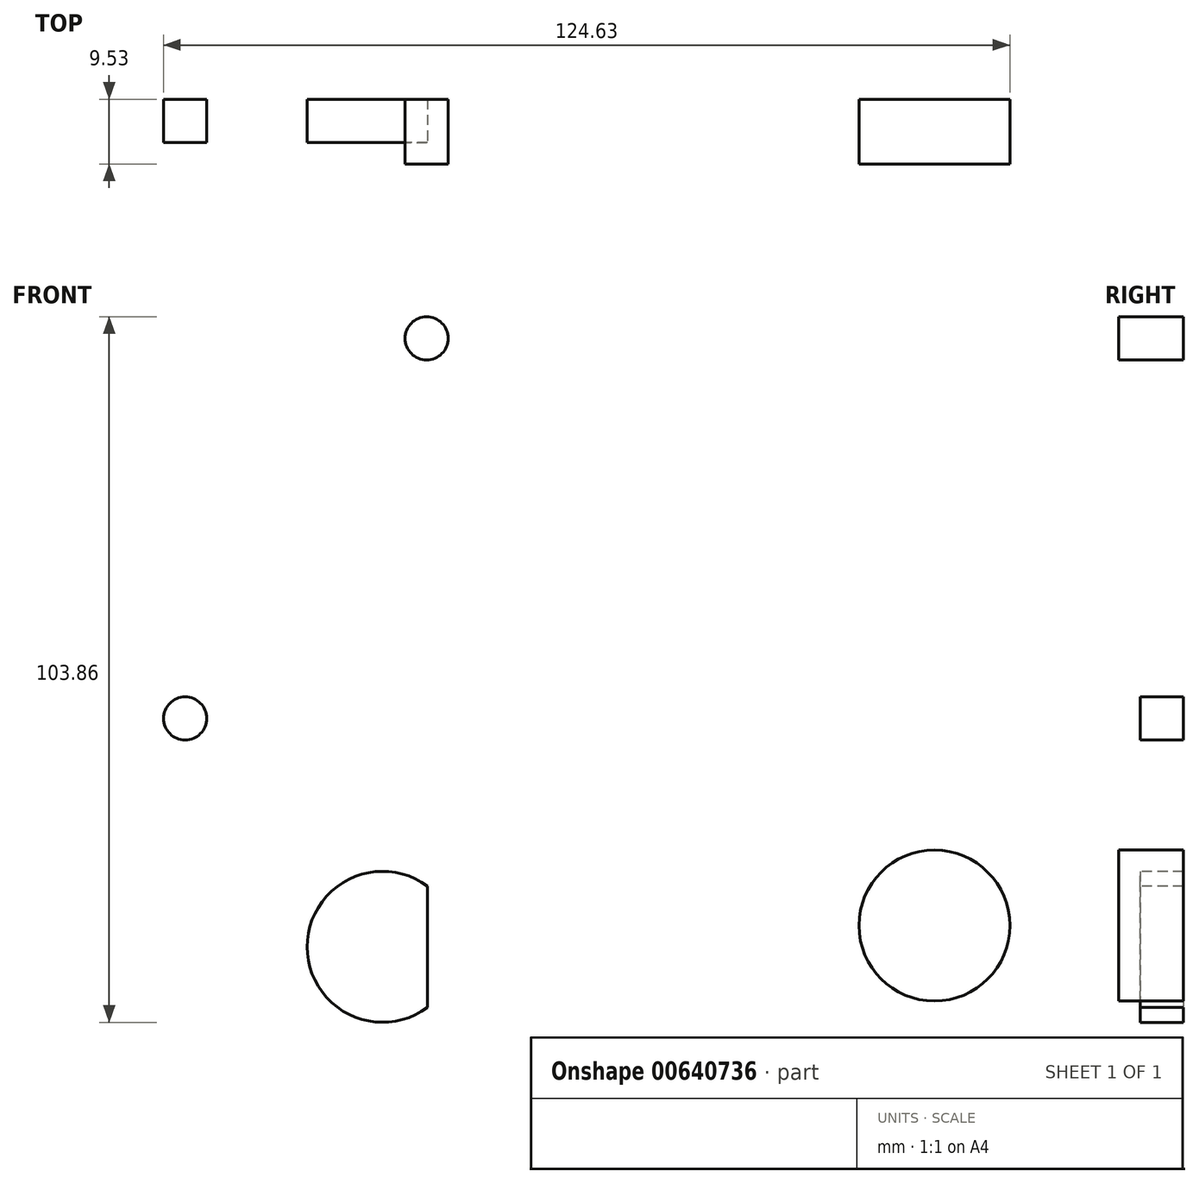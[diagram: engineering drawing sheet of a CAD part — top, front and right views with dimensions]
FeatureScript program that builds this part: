
annotation { "Feature Type Name" : "Feature", "Feature Type Description" : "" }
export const myFeature = defineFeature(function(context is Context, id is Id, definition is map)
    precondition{}
    {
        {
            var Q0;
            Q0=qCreatedBy(makeId("Front.planeOp"),FACE);
            var sketch = newSketch(context, id + "F0", { "sketchPlane" : qUnion([Q0])});
            skCircle(sketch, "E0", {"center": v(0, 0) * mm, "radius": 3.98 * mm});
            skCircle(sketch, "E1", {"center": v(0, 0) * mm, "radius": 15.88 * mm});
            skLineSegment(sketch, "E2", {"start": v(0, 0) * mm, "end": v(57.24, -66.17) * mm, "construction": true});
            skLineSegment(sketch, "E3", {"start": v(57.24, -66.17) * mm, "end": v(-41.54, 48.03) * mm, "construction": true});
            skCircle(sketch, "E4", {"center": v(-41.54, 48.03) * mm, "radius": 11.11 * mm});
            skCircle(sketch, "E5", {"center": v(-41.54, 48.03) * mm, "radius": 3.18 * mm});
            skCircle(sketch, "E6", {"center": v(33.23, -38.42) * mm, "radius": 11.11 * mm});
            skCircle(sketch, "E7", {"center": v(33.23, -38.42) * mm, "radius": 3.18 * mm});
            skCircle(sketch, "E8", {"center": v(26.2, -25.44) * mm, "radius": 3.18 * mm});
            skLineSegment(sketch, "E9", {"start": v(-41.54, 48.03) * mm, "end": v(-75.16, 18.95) * mm, "construction": true});
            skCircle(sketch, "E10", {"center": v(-75.16, 18.95) * mm, "radius": 7.94 * mm});
            skCircle(sketch, "E11", {"center": v(-75.16, 18.95) * mm, "radius": 3.18 * mm});
            skLineSegment(sketch, "E12", {"start": v(0, 0) * mm, "end": v(-79.13, -68.45) * mm, "construction": true});
            skCircle(sketch, "E13", {"center": v(-48.03, -41.54) * mm, "radius": 11.11 * mm});
            skCircle(sketch, "E14", {"center": v(-48.03, -41.54) * mm, "radius": 3.18 * mm});
            skCircle(sketch, "E15", {"center": v(-32.4, -28.03) * mm, "radius": 3.17 * mm});
            skLineSegment(sketch, "E16", {"start": v(-48.03, -41.54) * mm, "end": v(-94.65, 12.36) * mm, "construction": true});
            skCircle(sketch, "E17", {"center": v(-77.1, -7.93) * mm, "radius": 7.94 * mm});
            skCircle(sketch, "E18", {"center": v(-77.1, -7.93) * mm, "radius": 3.18 * mm});
            skLineSegment(sketch, "E19", {"start": v(-80.77, 24.56) * mm, "end": v(-49.4, 55.89) * mm});
            skLineSegment(sketch, "E20", {"start": v(-33.7, 55.9) * mm, "end": v(11.2, 11.26) * mm});
            skLineSegment(sketch, "E21", {"start": v(12.93, 9.21) * mm, "end": v(42.28, -31.97) * mm});
            skLineSegment(sketch, "E22", {"start": v(25.55, -46.45) * mm, "end": v(-10.98, -11.47) * mm});
            skPoint(sketch, "E23.endSnap0", {"position": v(-39.57, -34.23) * mm});
            skLineSegment(sketch, "E24", {"start": v(9.46, -12.75) * mm, "end": v(-41.4, -50.47) * mm});
            skLineSegment(sketch, "E25", {"start": v(-56.93, -48.2) * mm, "end": v(-83.46, -12.68) * mm});
            skLineSegment(sketch, "E26", {"start": v(-11.26, 11.2) * mm, "end": v(-42.42, -20.14) * mm});
            skPoint(sketch, "E26.startSnap0", {"position": v(-11.26, 33.58) * mm});
            skLineSegment(sketch, "E27", {"start": v(-71.49, -2.32) * mm, "end": v(-53.68, -20.15) * mm});
            skArc(sketch, "E28", {"start": v(-53.68, -20.15) * mm, "mid": v(-48.04, -22.49) * mm, "end": v(-42.42, -20.14) * mm});
            skLineSegment(sketch, "E29.trimOffspring", {"start": v(-55.32, -33.11) * mm, "end": v(-55.9, -33.7) * mm});
            skLineSegment(sketch, "E30", {"start": v(-69.36, 13.52) * mm, "end": v(-50.22, 27.74) * mm});
            skLineSegment(sketch, "E31", {"start": v(-12, -10.39) * mm, "end": v(-39.1, 26.1) * mm});
            skArc(sketch, "E32", {"start": v(-39.1, 26.1) * mm, "mid": v(-44.32, 29.22) * mm, "end": v(-50.22, 27.74) * mm});
            skLineSegment(sketch, "E33.trimOffspring", {"start": v(-49.97, 40.74) * mm, "end": v(-50.46, 41.4) * mm});
            skSolve(sketch);
        }
        {
            var Q0;
            {var subQ4=sQuery(id+"F0.wireOp",EDGE,"E19");Q0=makeQuery(id+"F0.imprint","IMPRINT",FACE,{"disambiguationData":[TD([[makeQuery(id+"F0.imprint","IMPRINT",EDGE,{"derivedFrom":subQ4}),-1.0]])]});}
            var Q1;
            Q1=makeQuery(id+"F0.imprint","IMPRINT",FACE,{"disambiguationData":[TD([[makeQuery(id+"F0.imprint","IMPRINT",EDGE,{"derivedFrom":sQuery(id+"F0.wireOp",EDGE,"E5")}),-1.0]])]});
            var Q2;
            Q2=makeQuery(id+"F0.imprint","IMPRINT",FACE,{"disambiguationData":[TD([[makeQuery(id+"F0.imprint","IMPRINT",EDGE,{"derivedFrom":sQuery(id+"F0.wireOp",EDGE,"E11")}),-1.0]])]});
            var Q3;
            Q3=makeQuery(id+"F0.imprint","IMPRINT",FACE,{"disambiguationData":[TD([[makeQuery(id+"F0.imprint","IMPRINT",EDGE,{"derivedFrom":sQuery(id+"F0.wireOp",EDGE,"E0")}),-1.0]])]});
            var Q4;
            {var subQ0=sQuery(id+"F0.wireOp",EDGE,"E26");var subQ1=sQuery(id+"F0.wireOp",EDGE,"E1");var subQ2=makeQuery(id+"F0.imprint","INTERSECT",VERTEX,{"derivedFrom":[subQ1,subQ0]});Q4=makeQuery(id+"F0.imprint","IMPRINT",FACE,{"disambiguationData":[TD([[makeQuery(id+"F0.imprint","IMPRINT",EDGE,{"disambiguationData":[TD([[subQ2,-1.0]])],"derivedFrom":subQ1}),-1.0]])]});}
            var Q5;
            {var subQ0=sQuery(id+"F0.wireOp",EDGE,"E22");var subQ1=sQuery(id+"F0.wireOp",EDGE,"E1");var subQ2=makeQuery(id+"F0.imprint","INTERSECT",VERTEX,{"derivedFrom":[subQ1,subQ0]});Q5=makeQuery(id+"F0.imprint","IMPRINT",FACE,{"disambiguationData":[TD([[makeQuery(id+"F0.imprint","IMPRINT",EDGE,{"disambiguationData":[TD([[subQ2,-1.0]])],"derivedFrom":subQ1}),-1.0]])]});}
            var Q6;
            Q6=makeQuery(id+"F0.imprint","IMPRINT",FACE,{"disambiguationData":[TD([[makeQuery(id+"F0.imprint","IMPRINT",EDGE,{"derivedFrom":sQuery(id+"F0.wireOp",EDGE,"E8")}),-1.0]])]});
            var Q7;
            Q7=makeQuery(id+"F0.imprint","IMPRINT",FACE,{"disambiguationData":[TD([[makeQuery(id+"F0.imprint","IMPRINT",EDGE,{"derivedFrom":sQuery(id+"F0.wireOp",EDGE,"E7")}),-1.0]])]});
            extrude(context, id + "F1", {"entities" : qUnion([Q0, Q1, Q2, Q3, Q4, Q5, Q6, Q7]), "depth" : 3.17 * mm, "offsetDistance" : 25.4 * mm});
        }
        {
            var Q0;
            Q0=makeQuery(id+"F0.imprint","IMPRINT",FACE,{"disambiguationData":[TD([[makeQuery(id+"F0.imprint","IMPRINT",EDGE,{"derivedFrom":sQuery(id+"F0.wireOp",EDGE,"E15")}),-1.0]])]});
            var Q1;
            Q1=makeQuery(id+"F0.imprint","IMPRINT",FACE,{"disambiguationData":[TD([[makeQuery(id+"F0.imprint","IMPRINT",EDGE,{"derivedFrom":sQuery(id+"F0.wireOp",EDGE,"E14")}),-1.0]])]});
            var Q2;
            Q2=makeQuery(id+"F0.imprint","IMPRINT",FACE,{"disambiguationData":[TD([[makeQuery(id+"F0.imprint","IMPRINT",EDGE,{"derivedFrom":sQuery(id+"F0.wireOp",EDGE,"E18")}),-1.0]])]});
            var Q3;
            {var subQ0=sQuery(id+"F0.wireOp",EDGE,"E22");var subQ1=sQuery(id+"F0.wireOp",EDGE,"E1");var subQ2=makeQuery(id+"F0.imprint","INTERSECT",VERTEX,{"derivedFrom":[subQ1,subQ0]});Q3=makeQuery(id+"F0.imprint","IMPRINT",FACE,{"disambiguationData":[TD([[makeQuery(id+"F0.imprint","IMPRINT",EDGE,{"disambiguationData":[TD([[subQ2,-1.0]])],"derivedFrom":subQ1}),-1.0]])]});}
            var Q4;
            Q4=makeQuery(id+"F0.imprint","IMPRINT",FACE,{"disambiguationData":[TD([[makeQuery(id+"F0.imprint","IMPRINT",EDGE,{"derivedFrom":sQuery(id+"F0.wireOp",EDGE,"E0")}),-1.0]])]});
            var Q5;
            {var subQ0=sQuery(id+"F0.wireOp",EDGE,"E26");var subQ1=sQuery(id+"F0.wireOp",EDGE,"E1");var subQ2=makeQuery(id+"F0.imprint","INTERSECT",VERTEX,{"derivedFrom":[subQ1,subQ0]});Q5=makeQuery(id+"F0.imprint","IMPRINT",FACE,{"disambiguationData":[TD([[makeQuery(id+"F0.imprint","IMPRINT",EDGE,{"disambiguationData":[TD([[subQ2,-1.0]])],"derivedFrom":subQ1}),-1.0]])]});}
            extrude(context, id + "F2", {"entities" : qUnion([Q0, Q1, Q2, Q3, Q4, Q5]), "oppositeDirection" : true, "depth" : 3.17 * mm, "offsetDistance" : 25.4 * mm});
        }
        {
            var Q0;
            Q0=qCreatedBy(makeId("Front.planeOp"),FACE);
            cPlane(context, id + "F3", {"entities" : qUnion([Q0]), "cplaneType" : CPlaneType.OFFSET, "offset" : 9.52 * mm, "oppositeDirection" : true, "width" : 152.4 * mm, "height" : 152.4 * mm});
        }
        {
            var Q0;
            Q0=makeQuery(id+"F2.opExtrude","CAP_FACE",FACE,{"disambiguationData":[OSD([sQuery(id+"F0.wireOp",EDGE,"E0"),sQuery(id+"F0.wireOp",EDGE,"E1"),sQuery(id+"F0.wireOp",EDGE,"E13"),sQuery(id+"F0.wireOp",EDGE,"E14"),sQuery(id+"F0.wireOp",EDGE,"E15"),sQuery(id+"F0.wireOp",EDGE,"E17"),sQuery(id+"F0.wireOp",EDGE,"E18"),sQuery(id+"F0.wireOp",EDGE,"E24"),sQuery(id+"F0.wireOp",EDGE,"E25"),sQuery(id+"F0.wireOp",EDGE,"E26"),sQuery(id+"F0.wireOp",EDGE,"E27"),sQuery(id+"F0.wireOp",EDGE,"E28"),sQuery(id+"F0.wireOp",EDGE,"E31")])],"isStart":false});
            var sketch = newSketch(context, id + "F4", { "sketchPlane" : qUnion([Q0])});
            skCircle(sketch, "E34", {"center": v(48.03, -41.54) * mm, "radius": 11.11 * mm});
            skLineSegment(sketch, "E35", {"start": v(41.4, -50.47) * mm, "end": v(41.4, -32.62) * mm});
            skSolve(sketch);
        }
        {
            var Q0;
            {var subQ0=sQuery(id+"F4.wireOp",EDGE,"E35");Q0=makeQuery(id+"F4.imprint","IMPRINT",FACE,{"disambiguationData":[TD([[makeQuery(id+"F4.imprint","IMPRINT",EDGE,{"derivedFrom":subQ0}),-1.0]])]});}
            var Q1;
            Q1=makeQuery(id+"F4.imprint","IMPRINT",FACE,{"disambiguationData":[TD([[makeQuery(id+"F4.imprint","IMPRINT",EDGE,{"derivedFrom":makeQuery(id+"F2.opExtrude","CAP_EDGE",EDGE,{"disambiguationData":[OSD([sQuery(id+"F0.wireOp",EDGE,"E14")])],"isStart":false})}),-1.0]])]});
            var Q2;
            Q2=makeQuery(id+"F0.imprint","IMPRINT",FACE,{"disambiguationData":[TD([[makeQuery(id+"F0.imprint","IMPRINT",EDGE,{"derivedFrom":sQuery(id+"F0.wireOp",EDGE,"E7")}),-1.0]])]});
            var Q3;
            Q3=makeQuery(id+"F0.imprint","IMPRINT",FACE,{"disambiguationData":[TD([[makeQuery(id+"F0.imprint","IMPRINT",EDGE,{"derivedFrom":sQuery(id+"F0.wireOp",EDGE,"E7")}),1.0]])]});
            var Q4;
            Q4=makeQuery(id+"F0.imprint","IMPRINT",FACE,{"disambiguationData":[TD([[makeQuery(id+"F0.imprint","IMPRINT",EDGE,{"derivedFrom":sQuery(id+"F0.wireOp",EDGE,"E5")}),1.0]])]});
            var Q5;
            Q5=makeQuery(id+"F4.imprint","IMPRINT",FACE,{"disambiguationData":[TD([[makeQuery(id+"F4.imprint","IMPRINT",EDGE,{"derivedFrom":makeQuery(id+"F2.opExtrude","CAP_EDGE",EDGE,{"disambiguationData":[OSD([sQuery(id+"F0.wireOp",EDGE,"E18")])],"isStart":false})}),-1.0]])]});
            var Q6;
            Q6=qCreatedBy(id+"F3.planeOp",FACE);
            extrude(context, id + "F5", {"entities" : qUnion([Q0, Q1, Q2, Q3, Q4, Q5]), "endBound" : BoundingType.UP_TO_SURFACE, "depth" : 25.4 * mm, "endBoundEntityFace" : qUnion([Q6]), "offsetDistance" : 25.4 * mm});
        }
        {
            var Q0;
            Q0=makeQuery(id+"F1.opExtrude","SWEPT_BODY",BODY,{"disambiguationData":[OSD([sQuery(id+"F0.wireOp",EDGE,"E0"),sQuery(id+"F0.wireOp",EDGE,"E1"),sQuery(id+"F0.wireOp",EDGE,"E4"),sQuery(id+"F0.wireOp",EDGE,"E5"),sQuery(id+"F0.wireOp",EDGE,"E6"),sQuery(id+"F0.wireOp",EDGE,"E7"),sQuery(id+"F0.wireOp",EDGE,"E8"),sQuery(id+"F0.wireOp",EDGE,"E10"),sQuery(id+"F0.wireOp",EDGE,"E11"),sQuery(id+"F0.wireOp",EDGE,"E19"),sQuery(id+"F0.wireOp",EDGE,"E20"),sQuery(id+"F0.wireOp",EDGE,"E21"),sQuery(id+"F0.wireOp",EDGE,"E22"),sQuery(id+"F0.wireOp",EDGE,"E30"),sQuery(id+"F0.wireOp",EDGE,"E31"),sQuery(id+"F0.wireOp",EDGE,"E32")])]});
            var Q1;
            Q1=makeQuery(id+"F2.opExtrude","SWEPT_BODY",BODY,{"disambiguationData":[OSD([sQuery(id+"F0.wireOp",EDGE,"E0"),sQuery(id+"F0.wireOp",EDGE,"E1"),sQuery(id+"F0.wireOp",EDGE,"E13"),sQuery(id+"F0.wireOp",EDGE,"E14"),sQuery(id+"F0.wireOp",EDGE,"E15"),sQuery(id+"F0.wireOp",EDGE,"E17"),sQuery(id+"F0.wireOp",EDGE,"E18"),sQuery(id+"F0.wireOp",EDGE,"E24"),sQuery(id+"F0.wireOp",EDGE,"E25"),sQuery(id+"F0.wireOp",EDGE,"E26"),sQuery(id+"F0.wireOp",EDGE,"E27"),sQuery(id+"F0.wireOp",EDGE,"E28"),sQuery(id+"F0.wireOp",EDGE,"E31")])]});
            var Q2;
            Q2=makeQuery(id+"F5.opExtrude","SWEPT_BODY",BODY,{"disambiguationData":[OSD([sQuery(id+"F0.wireOp",EDGE,"E5")])]});
            var Q3;
            Q3=makeQuery(id+"F5.opExtrude","SWEPT_BODY",BODY,{"disambiguationData":[OSD([sQuery(id+"F0.wireOp",EDGE,"E18")])]});
            var Q4;
            Q4=makeQuery(id+"F5.opExtrude","SWEPT_BODY",BODY,{"disambiguationData":[OSD([sQuery(id+"F4.wireOp",EDGE,"E34"),sQuery(id+"F4.wireOp",EDGE,"E35")])]});
            var Q5;
            Q5=makeQuery(id+"F5.opExtrude","SWEPT_BODY",BODY,{"disambiguationData":[OSD([sQuery(id+"F0.wireOp",EDGE,"E6")])]});
            booleanBodies(context, id + "F6", {"operationType" : BooleanOperationType.SUBTRACTION, "tools" : qUnion([Q0, Q1]), "targets" : qUnion([Q2, Q3, Q4, Q5])});
        }
    });
